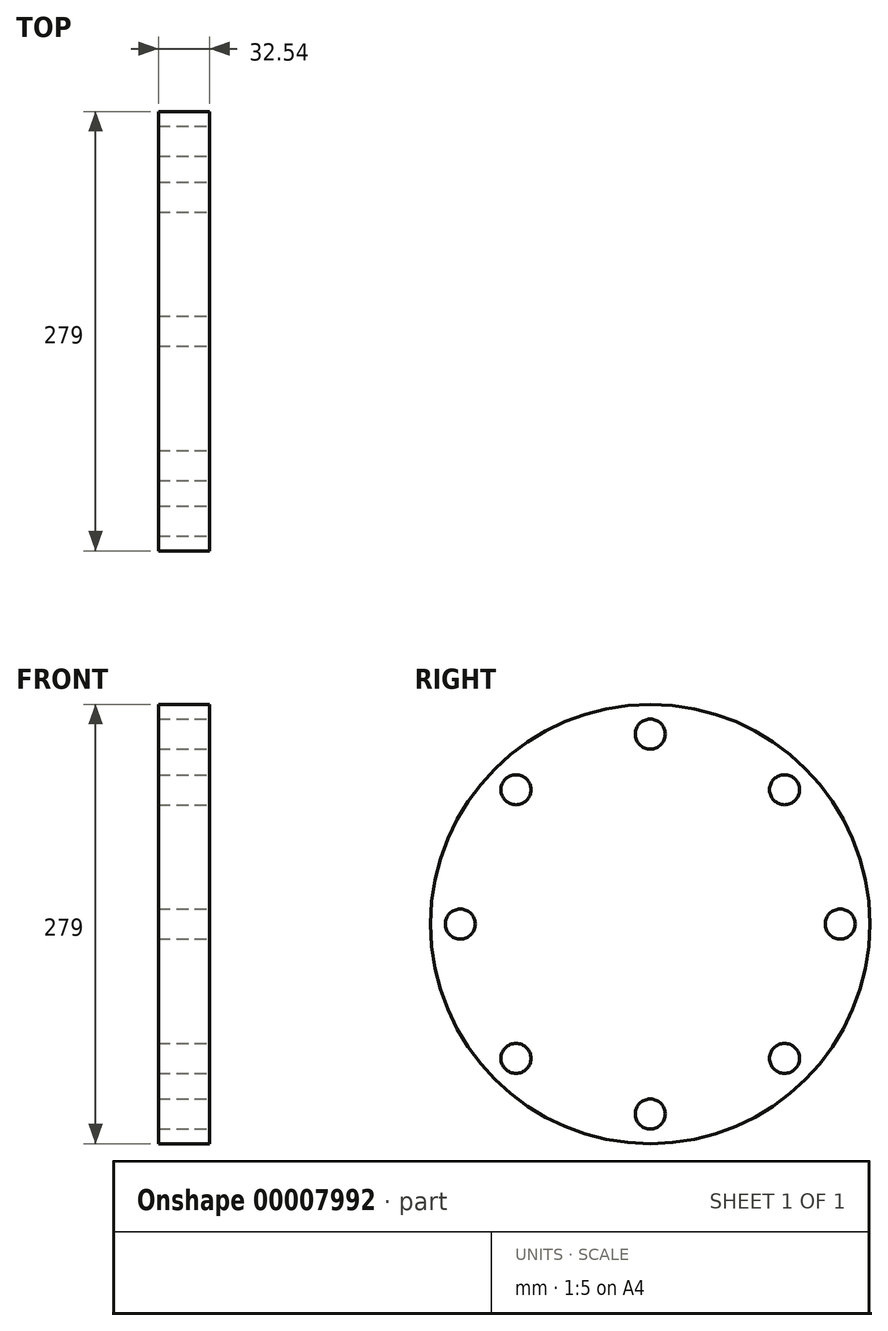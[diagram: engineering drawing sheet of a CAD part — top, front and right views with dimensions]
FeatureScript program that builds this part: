
annotation { "Feature Type Name" : "Feature", "Feature Type Description" : "" }
export const myFeature = defineFeature(function(context is Context, id is Id, definition is map)
    precondition{}
    {
        {
            var Q0;
            Q0=qCreatedBy(makeId("Front.planeOp"),FACE);
            var sketch = newSketch(context, id + "F0", { "sketchPlane" : qUnion([Q0])});
            skLineSegment(sketch, "E0", {"start": v(0, 0) * mm, "end": v(-236.85, 0) * mm, "construction": true});
            skLineSegment(sketch, "E1", {"start": v(0, 0) * mm, "end": v(0, 139.5) * mm});
            skLineSegment(sketch, "E2", {"start": v(0, 139.5) * mm, "end": v(32.54, 139.5) * mm});
            skLineSegment(sketch, "E3", {"start": v(32.54, 139.5) * mm, "end": v(32.54, 0) * mm});
            skLineSegment(sketch, "E4", {"start": v(32.54, 0) * mm, "end": v(0, 0) * mm});
            skSolve(sketch);
        }
        {
            var Q0;
            Q0=makeQuery(id+"F0.imprint","IMPRINT",FACE,{"disambiguationData":[TD([[makeQuery(id+"F0.imprint","IMPRINT",EDGE,{"derivedFrom":sQuery(id+"F0.wireOp",EDGE,"2daf891e-ae0d-41c8-a188-7f40d70cd6d6")}),-1.0]])]});
            var Q1;
            Q1=makeQuery(id+"F0.imprint","IMPRINT",FACE,{"disambiguationData":[TD([[makeQuery(id+"F0.imprint","IMPRINT",EDGE,{"derivedFrom":sQuery(id+"F0.wireOp",EDGE,"E1")}),-1.0]])]});
            var Q2;
            Q2=sQuery(id+"F0.wireOp",EDGE,"E0");
            revolve(context, id + "F1", {"entities" : qUnion([Q0, Q1]), "axis" : qUnion([Q2]), "revolveType" : RevolveType.FULL});
        }
        {
            var Q0;
            Q0=makeQuery(id+"F1.opRevolve","SWEPT_FACE",FACE,{"disambiguationData":[OSD([sQuery(id+"F0.wireOp",EDGE,"E3")])]});
            var sketch = newSketch(context, id + "F2", { "sketchPlane" : qUnion([Q0])});
            skCircle(sketch, "E5", {"center": v(0, 120.65) * mm, "radius": 9.53 * mm});
            skCircle(sketch, "E6.1.0", {"center": v(-85.31, 85.31) * mm, "radius": 9.53 * mm});
            skCircle(sketch, "E6.2.0", {"center": v(-120.65, 0) * mm, "radius": 9.53 * mm});
            skCircle(sketch, "E6.3.0", {"center": v(-85.31, -85.31) * mm, "radius": 9.53 * mm});
            skCircle(sketch, "E6.4.0", {"center": v(0, -120.65) * mm, "radius": 9.53 * mm});
            skCircle(sketch, "E6.5.0", {"center": v(85.31, -85.31) * mm, "radius": 9.53 * mm});
            skCircle(sketch, "E6.6.0", {"center": v(120.65, 0) * mm, "radius": 9.53 * mm});
            skCircle(sketch, "E6.7.0", {"center": v(85.31, 85.31) * mm, "radius": 9.53 * mm});
            skPoint(sketch, "E6.center", {"position": v(0, 0) * mm});
            skSolve(sketch);
        }
        {
            var Q0;
            Q0=makeQuery(id+"F2.imprint","IMPRINT",FACE,{"disambiguationData":[TD([[makeQuery(id+"F2.imprint","IMPRINT",EDGE,{"derivedFrom":sQuery(id+"F2.wireOp",EDGE,"E6.1.0")}),1.0]])]});
            var Q1;
            Q1=makeQuery(id+"F2.imprint","IMPRINT",FACE,{"disambiguationData":[TD([[makeQuery(id+"F2.imprint","IMPRINT",EDGE,{"derivedFrom":sQuery(id+"F2.wireOp",EDGE,"E5")}),1.0]])]});
            var Q2;
            Q2=makeQuery(id+"F2.imprint","IMPRINT",FACE,{"disambiguationData":[TD([[makeQuery(id+"F2.imprint","IMPRINT",EDGE,{"derivedFrom":sQuery(id+"F2.wireOp",EDGE,"E6.7.0")}),1.0]])]});
            var Q3;
            Q3=makeQuery(id+"F2.imprint","IMPRINT",FACE,{"disambiguationData":[TD([[makeQuery(id+"F2.imprint","IMPRINT",EDGE,{"derivedFrom":sQuery(id+"F2.wireOp",EDGE,"E6.6.0")}),1.0]])]});
            var Q4;
            Q4=makeQuery(id+"F2.imprint","IMPRINT",FACE,{"disambiguationData":[TD([[makeQuery(id+"F2.imprint","IMPRINT",EDGE,{"derivedFrom":sQuery(id+"F2.wireOp",EDGE,"E6.5.0")}),1.0]])]});
            var Q5;
            Q5=makeQuery(id+"F2.imprint","IMPRINT",FACE,{"disambiguationData":[TD([[makeQuery(id+"F2.imprint","IMPRINT",EDGE,{"derivedFrom":sQuery(id+"F2.wireOp",EDGE,"E6.4.0")}),1.0]])]});
            var Q6;
            Q6=makeQuery(id+"F2.imprint","IMPRINT",FACE,{"disambiguationData":[TD([[makeQuery(id+"F2.imprint","IMPRINT",EDGE,{"derivedFrom":sQuery(id+"F2.wireOp",EDGE,"E6.3.0")}),1.0]])]});
            var Q7;
            Q7=makeQuery(id+"F2.imprint","IMPRINT",FACE,{"disambiguationData":[TD([[makeQuery(id+"F2.imprint","IMPRINT",EDGE,{"derivedFrom":sQuery(id+"F2.wireOp",EDGE,"E6.2.0")}),1.0]])]});
            var Q8;
            Q8=makeQuery(id+"F1.opRevolve","SWEPT_FACE",FACE,{"disambiguationData":[OSD([sQuery(id+"F0.wireOp",EDGE,"E3")])]});
            extrude(context, id + "F3", {"entities" : qUnion([Q0, Q1, Q2, Q3, Q4, Q5, Q6, Q7]), "operationType" : NewBodyOperationType.REMOVE, "endBound" : BoundingType.UP_TO_BODY, "oppositeDirection" : true, "endBoundEntityBody" : qUnion([Q8]), "depth" : 25 * mm});
        }
    });
